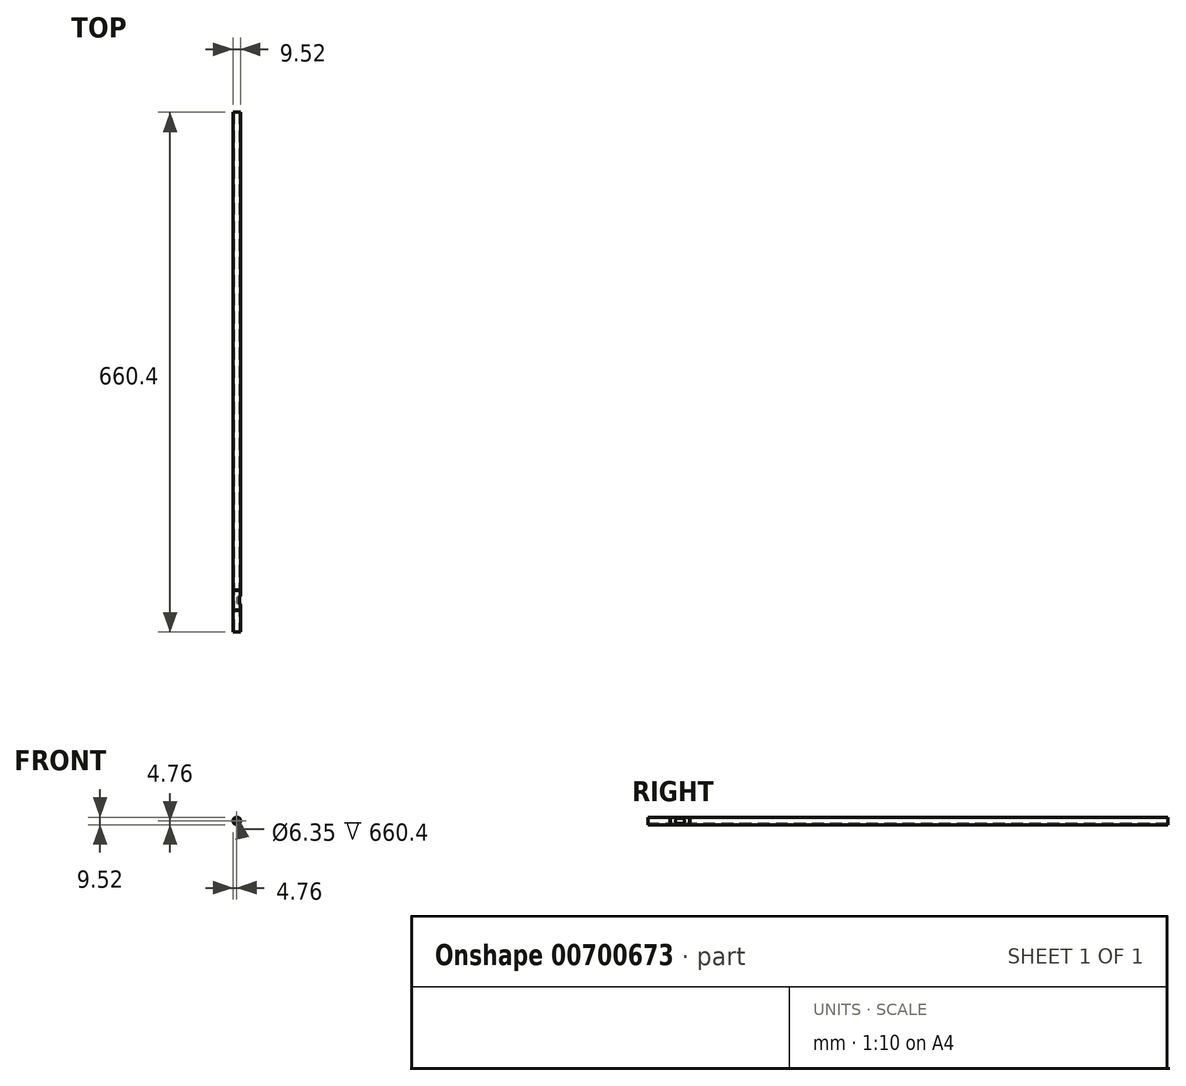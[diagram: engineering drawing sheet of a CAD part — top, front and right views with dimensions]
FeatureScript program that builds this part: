
annotation { "Feature Type Name" : "Feature", "Feature Type Description" : "" }
export const myFeature = defineFeature(function(context is Context, id is Id, definition is map)
    precondition{}
    {
        {
            var Q0;
            Q0=qCreatedBy(makeId("Front.planeOp"),FACE);
            var sketch = newSketch(context, id + "F0", { "sketchPlane" : qUnion([Q0])});
            skCircle(sketch, "E0", {"center": v(0, 0) * mm, "radius": 3.18 * mm});
            skCircle(sketch, "E1", {"center": v(0, 0) * mm, "radius": 4.76 * mm});
            skSolve(sketch);
        }
        {
            var Q0;
            Q0 = qSketchRegion(id + "F0", true);
            extrude(context, id + "F1", {"entities" : qUnion([Q0]), "oppositeDirection" : true, "depth" : 660.4 * mm, "offsetDistance" : 25.4 * mm});
        }
        {
            var Q0;
            Q0=qCreatedBy(makeId("Right.planeOp"),FACE);
            var sketch = newSketch(context, id + "F2", { "sketchPlane" : qUnion([Q0])});
            skPoint(sketch, "E2", {"position": v(38.1, 0) * mm});
            skArc(sketch, "E3", {"start": v(38.1, 3.3) * mm, "mid": v(34.8, 0) * mm, "end": v(38.1, -3.3) * mm});
            skArc(sketch, "E4", {"start": v(43.18, -3.3) * mm, "mid": v(46.48, 0) * mm, "end": v(43.18, 3.3) * mm});
            skLineSegment(sketch, "E5", {"start": v(38.1, -3.3) * mm, "end": v(43.18, -3.3) * mm});
            skLineSegment(sketch, "E6", {"start": v(43.18, 3.3) * mm, "end": v(38.1, 3.3) * mm});
            skSolve(sketch);
        }
        {
            var Q0;
            Q0 = qSketchRegion(id + "F2", true);
            extrude(context, id + "F3", {"entities" : qUnion([Q0]), "operationType" : NewBodyOperationType.REMOVE, "depth" : 25.4 * mm, "offsetDistance" : 25.4 * mm});
        }
        {
            var Q0;
            Q0=qCreatedBy(makeId("Right.planeOp"),FACE);
            var sketch = newSketch(context, id + "F4", { "sketchPlane" : qUnion([Q0])});
            skLineSegment(sketch, "E7.bottom", {"start": v(28.45, -3.97) * mm, "end": v(27.65, -3.97) * mm});
            skLineSegment(sketch, "E7.top", {"start": v(28.45, -4.76) * mm, "end": v(27.65, -4.76) * mm});
            skLineSegment(sketch, "E7.left", {"start": v(28.45, -3.97) * mm, "end": v(28.45, -4.76) * mm});
            skLineSegment(sketch, "E7.right", {"start": v(27.65, -3.97) * mm, "end": v(27.65, -4.76) * mm});
            skLineSegment(sketch, "E8", {"start": v(660.4, -4.76) * mm, "end": v(0, -4.76) * mm});
            skLineSegment(sketch, "E9.bottom", {"start": v(52.83, -3.97) * mm, "end": v(53.63, -3.97) * mm});
            skLineSegment(sketch, "E9.top", {"start": v(52.83, -4.76) * mm, "end": v(53.63, -4.76) * mm});
            skLineSegment(sketch, "E9.left", {"start": v(52.83, -3.97) * mm, "end": v(52.83, -4.76) * mm});
            skLineSegment(sketch, "E9.right", {"start": v(53.63, -3.97) * mm, "end": v(53.63, -4.76) * mm});
            skSolve(sketch);
        }
        {
            var Q0;
            Q0 = qSketchRegion(id + "F4", true);
            var Q1;
            Q1=makeQuery(id+"F1.opExtrude","CAP_EDGE",EDGE,{"disambiguationData":[OSD([sQuery(id+"F0.wireOp",EDGE,"E0")])],"isStart":true});
            revolve(context, id + "F5", {"operationType" : NewBodyOperationType.REMOVE, "entities" : qUnion([Q0]), "axis" : qUnion([Q1]), "revolveType" : RevolveType.FULL, "oppositeDirection" : true});
        }
    });
